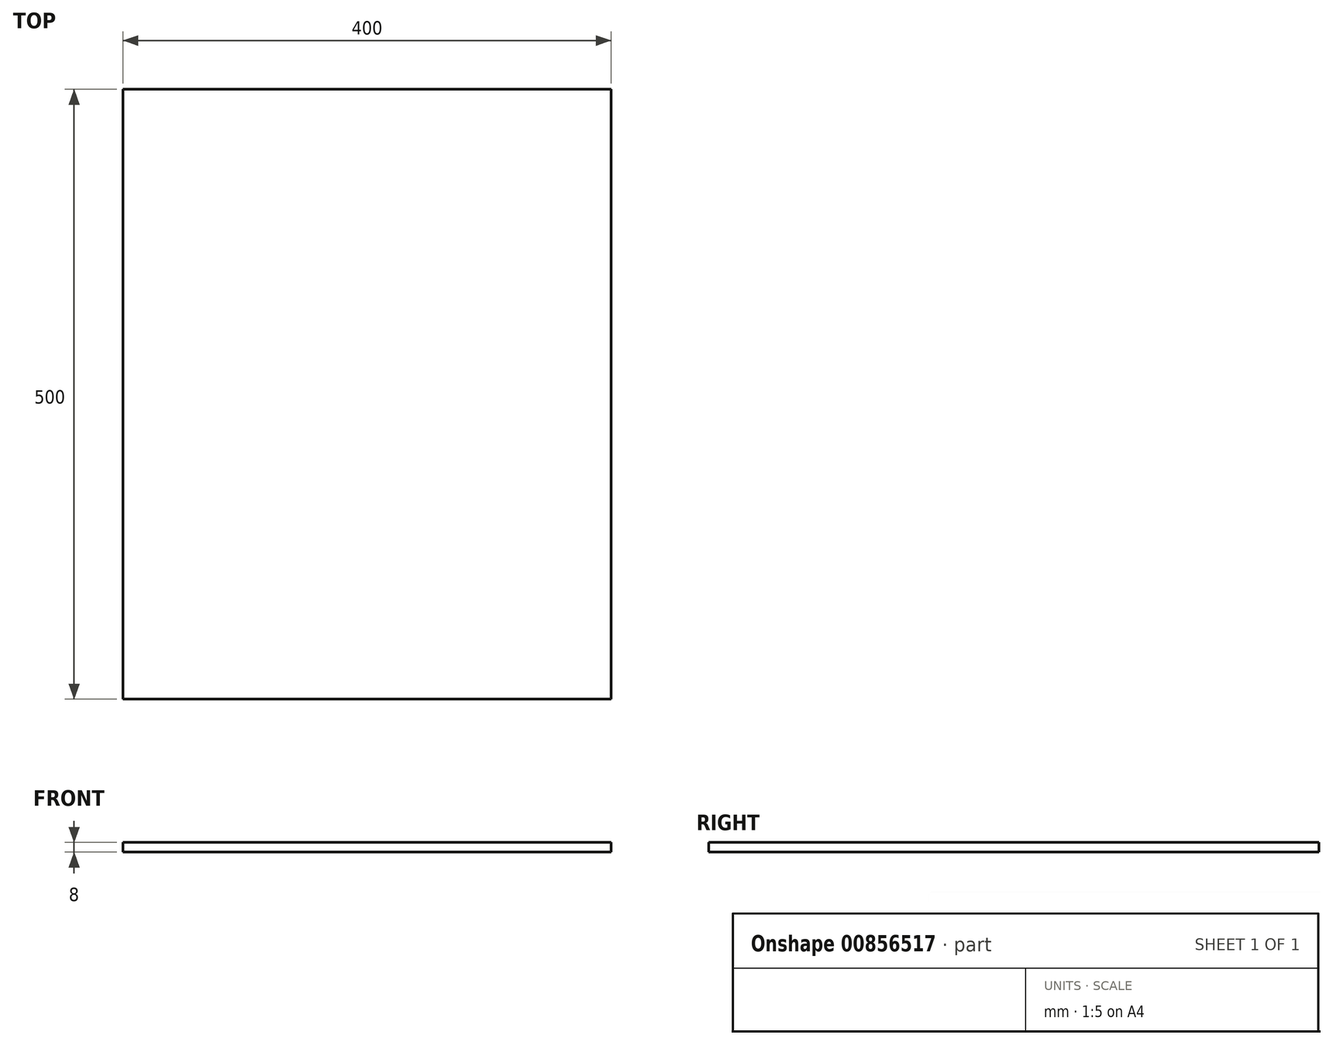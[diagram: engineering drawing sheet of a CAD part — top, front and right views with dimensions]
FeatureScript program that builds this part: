
annotation { "Feature Type Name" : "Feature", "Feature Type Description" : "" }
export const myFeature = defineFeature(function(context is Context, id is Id, definition is map)
    precondition{}
    {
        {
            var Q0;
            Q0=qCreatedBy(makeId("Top.planeOp"),FACE);
            var sketch = newSketch(context, id + "F0", { "sketchPlane" : qUnion([Q0])});
            skLineSegment(sketch, "E0.bottom", {"start": v(200, 251.73) * mm, "end": v(-200, 251.73) * mm});
            skLineSegment(sketch, "E0.top", {"start": v(200, -248.27) * mm, "end": v(-200, -248.27) * mm});
            skLineSegment(sketch, "E0.left", {"start": v(200, 251.73) * mm, "end": v(200, -248.27) * mm});
            skLineSegment(sketch, "E0.right", {"start": v(-200, 251.73) * mm, "end": v(-200, -248.27) * mm});
            skPoint(sketch, "E0.middle", {"position": v(0, 1.73) * mm});
            skSolve(sketch);
        }
        {
            var Q0;
            Q0=makeQuery(id+"F0.imprint","IMPRINT",FACE,{"disambiguationData":[TD([[makeQuery(id+"F0.imprint","IMPRINT",EDGE,{"derivedFrom":sQuery(id+"F0.wireOp",EDGE,"E0.bottom")}),1.0]])]});
            extrude(context, id + "F1", {"entities" : qUnion([Q0]), "depth" : 8 * mm, "offsetDistance" : 25 * mm});
        }
    });
